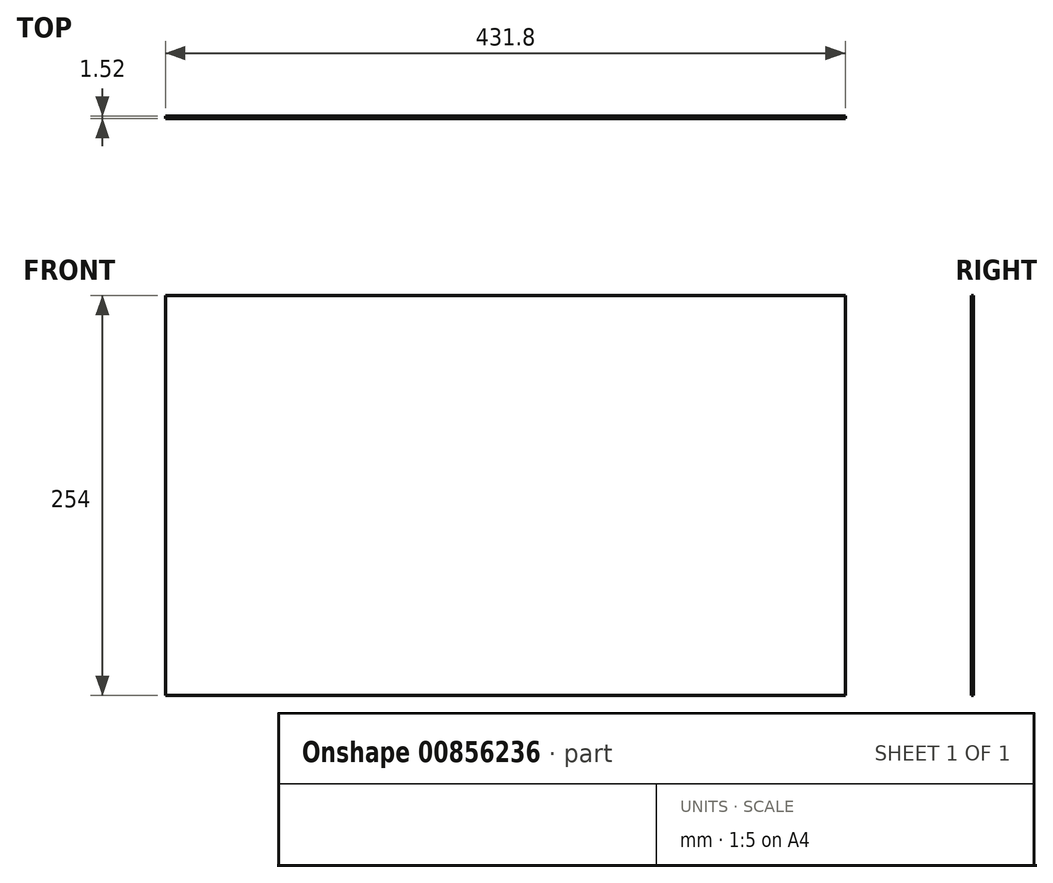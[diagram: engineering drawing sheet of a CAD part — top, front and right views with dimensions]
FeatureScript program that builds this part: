
annotation { "Feature Type Name" : "Feature", "Feature Type Description" : "" }
export const myFeature = defineFeature(function(context is Context, id is Id, definition is map)
    precondition{}
    {
        {
            var Q0;
            Q0=qCreatedBy(makeId("Front.planeOp"),FACE);
            var sketch = newSketch(context, id + "F0", { "sketchPlane" : qUnion([Q0])});
            skLineSegment(sketch, "E0.bottom", {"start": v(0, 0) * mm, "end": v(431.8, 0) * mm});
            skLineSegment(sketch, "E0.top", {"start": v(0, 254) * mm, "end": v(431.8, 254) * mm});
            skLineSegment(sketch, "E0.left", {"start": v(0, 0) * mm, "end": v(0, 254) * mm});
            skLineSegment(sketch, "E0.right", {"start": v(431.8, 0) * mm, "end": v(431.8, 254) * mm});
            skSolve(sketch);
        }
        {
            var Q0;
            Q0 = qSketchRegion(id + "F0", true);
            extrude(context, id + "F1", {"entities" : qUnion([Q0]), "depth" : 1.52 * mm, "offsetDistance" : 25.4 * mm});
        }
    });
